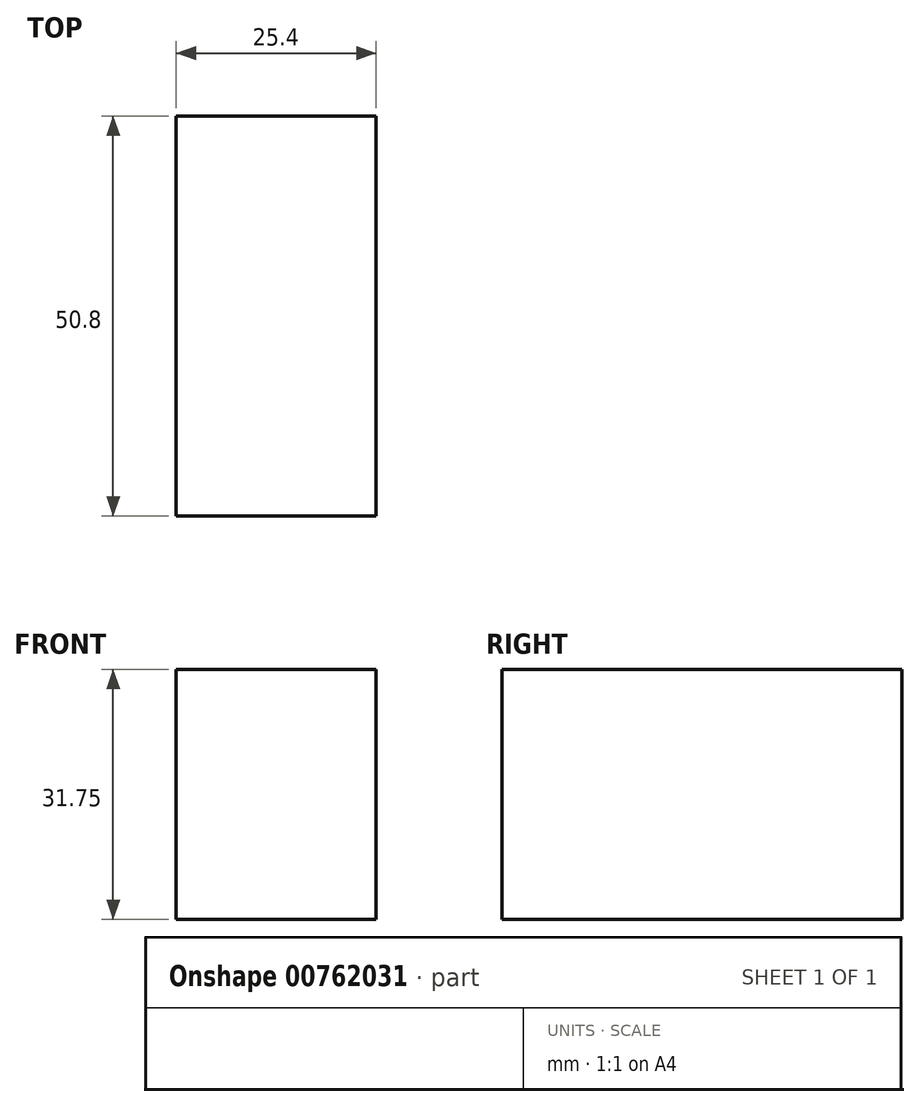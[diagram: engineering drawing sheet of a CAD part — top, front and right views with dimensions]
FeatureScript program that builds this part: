
annotation { "Feature Type Name" : "Feature", "Feature Type Description" : "" }
export const myFeature = defineFeature(function(context is Context, id is Id, definition is map)
    precondition{}
    {
        {
            var Q0;
            Q0=qCreatedBy(makeId("Right.planeOp"),FACE);
            var sketch = newSketch(context, id + "F0", { "sketchPlane" : qUnion([Q0])});
            skLineSegment(sketch, "E0", {"start": v(0, 0) * mm, "end": v(0, 31.75) * mm});
            skLineSegment(sketch, "E1", {"start": v(0, 31.75) * mm, "end": v(50.8, 31.75) * mm});
            skLineSegment(sketch, "E2", {"start": v(50.8, 31.75) * mm, "end": v(50.8, 0) * mm});
            skLineSegment(sketch, "E3", {"start": v(50.8, 0) * mm, "end": v(0, 0) * mm});
            skSolve(sketch);
        }
        {
            var Q0;
            Q0 = qSketchRegion(id + "F0", true);
            extrude(context, id + "F1", {"entities" : qUnion([Q0]), "depth" : 25.4 * mm, "offsetDistance" : 25.4 * mm});
        }
    });
